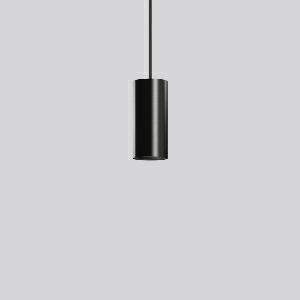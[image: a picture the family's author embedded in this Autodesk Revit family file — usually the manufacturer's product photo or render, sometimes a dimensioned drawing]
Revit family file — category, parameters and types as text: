
# Revit family: deecos_p_mini_911520_003_1_721f
name_source: partatom
category: Lighting Fixtures
units: mm (PartAtom-declared; Revit-internal decimal feet)

## family parameters
Cut with Voids When Loaded = No
Host = Face
Light Source = No
Part Type = Normal
Room Calculation Point = No
Round Connector Dimension = Use Diameter
Shared = No

## types (1)
- DEECOS P mini (1 x LED Modul 940, 2050 lm, 4000)
    Apparent Load = 20 VA
    Approval mark = CE
    CIE Flux Codes = 95 100 100 100 100
    Color Rendering = 92
    Color Temperature = 4000
    Default Elevation = 1800 mm
    Description = Series: DEECOS P mini
Cylindrical pendant luminaire. Housing: die-cast aluminium, powder-coated. Canopy made of powder-coated sheet steel with magnetic attachment. Optical assembly with lens made of plastic (polycarbonate) for the best homogeneous light distribution - can be changed without tools. Oval light distribution for corridor. Best colour rendering index Ra>90. Transparent pendant cable 5 m, can be shortened, with integrated steel cable. High quality converter without flickering and stroboscopic effect. The following accessories can be mounted without use of tools: interchangeable lenses, honeycomb louvre, clear and frosted diffusers, white interchangeable plastic ring. Decorative recessed suspension set available as accessory.Suitable for accessory Deecos P Tube cylinder extensions 0.5 m, 0.75 m or 1 m. 
Colour: deep black, matt (RAL 9005)
Diameter: 87 mm
Height: 195 mm
Suspension length: 5000 mm
Lamp: LED
Socket: without socket
Colour temperature: 4000K
Colour rendering index (CRI): 92
System power: 20 W
Rated luminous flux: 2050 lm
Luminous efficiency: 103 lm/W
Control gear: Regulated power supply
Protection class: I
Type of protection: IP 20
    Height = 195 mm
    Lamp = 1 x LED Modul 940
    Lamp Light Flux = 2050 lm
    Lamp count = 1
    Length = 87 mm
    Lifetime = 50000 h
    Luminous efficacy = 103 lm/W
    Manufacturer = RZB
    ModVariant = No
    Model = 911520.003.1
    Mounting Place = Ceiling
    Mounting Type = Pendant
    Number of Poles = 1
    OnlyDefault = Yes
    Power Factor = 1
    Product Name = DEECOS P mini
    Product group = Pendant luminaires
    ProductGroupID = 902
    Protection Class = Protection class I
    Protection Degree = IP 20
    RLX_Detail_Level = 1
    RLX_Emergency_Light_Flux = 0 lm
    RLX_Emergency_Type = 0
    RLX_Emergency_Type_DB = No
    RlxData = <blob elided: 64533 chars, md5=c9bd7bd3>
    Socket = socket
    Standby Power = 0 W
    System Light Flux = 2050 lm
    System Power = 20 W
    Type Comments = Product without accessories
    Type Image = 911476.003.jpg
    URL = http://relux.com
    VarID = ---
    Voltage = 230 V
    Voltage Range = 220-240 V
    Weight = 0.00 kg
    Width = 0 mm  [stored 0 ft]

note: [stored X ft] marks values corroborated as IEEE doubles in the binary element streams (Revit-internal decimal feet)

## geometry (parser evidence)
native form markers: Blend x4, Sweep x13
no freeform markers — native parametric forms only
